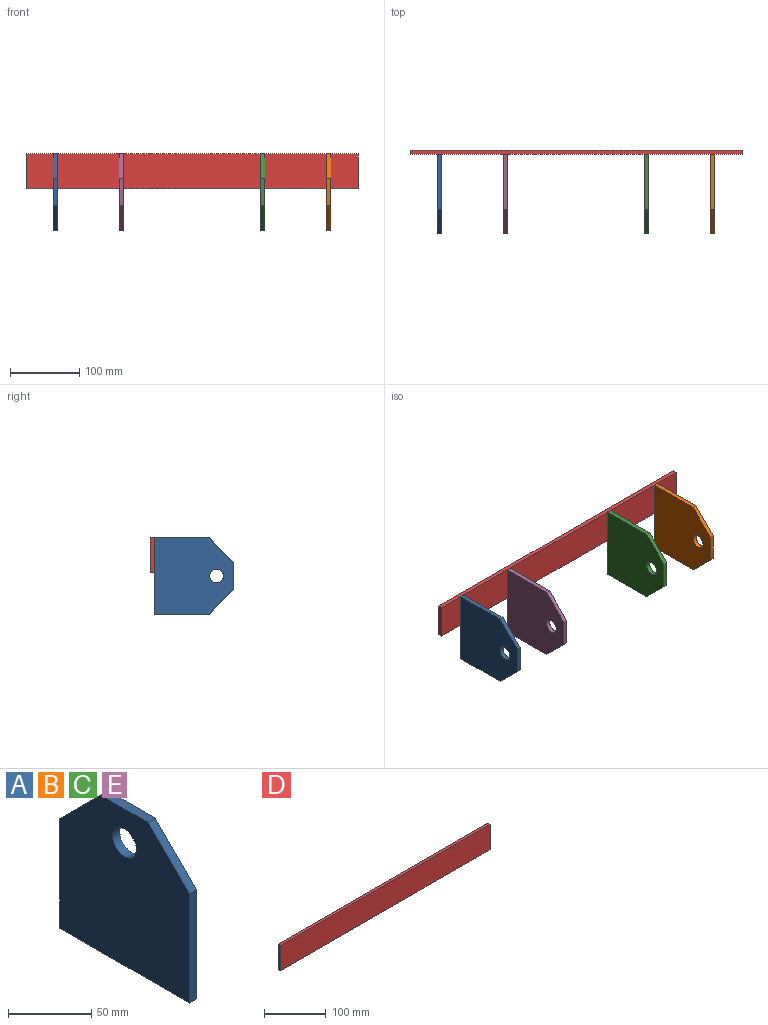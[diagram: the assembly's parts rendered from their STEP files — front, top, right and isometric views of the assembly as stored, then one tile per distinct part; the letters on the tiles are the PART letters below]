
ASSEMBLY  parts=5 mates=4
PART A: 9 faces, bbox 6x110x115 mm
  f0: plane 40x6mm, normal (0,0,1), area 240mm2, adj f1,f5,f7,f8
  f1: plane 35x35mm, normal (0,-0.71,0.71), area 297mm2, adj f0,f2,f7,f8
  f2: plane 80x6mm, normal (0,-1,0), area 480mm2, adj f1,f3,f7,f8
  f3: plane 110x6mm, normal (0,0,-1), area 660mm2, adj f2,f4,f7,f8
  f4: plane 80x6mm, normal (0,1,0), area 480mm2, adj f3,f5,f7,f8
  f5: plane 35x35mm, normal (0,0.71,0.71), area 297mm2, adj f0,f4,f7,f8
  f6: cylinder r=10mm len=20mm, axis (-1,0,0), area 377mm2, adj f7,f8
  f7: plane 115x110mm, normal (1,0,0), area 11110.8mm2, adj f0,f1,f2,f3,f4,f5,f6
  f8: plane 115x110mm, normal (-1,0,0), area 11110.8mm2, adj f0,f1,f2,f3,f4,f5,f6
PART B: same geometry as A
PART C: same geometry as A
PART D: 6 faces, bbox 480x6x50 mm
  f0: plane 480x6mm, normal (0,0,1), area 2880mm2, adj f1,f3,f4,f5
  f1: plane 50x6mm, normal (-1,0,0), area 300mm2, adj f0,f2,f4,f5
  f2: plane 480x6mm, normal (0,0,-1), area 2880mm2, adj f1,f3,f4,f5
  f3: plane 50x6mm, normal (1,0,0), area 300mm2, adj f0,f2,f4,f5
  f4: plane 480x50mm, normal (0,-1,0), area 24000mm2, adj f0,f1,f2,f3
  f5: plane 480x50mm, normal (0,1,0), area 24000mm2, adj f0,f1,f2,f3
PART E: same geometry as A
PLACE A rot(axis=(1,0,0),90deg) t=(-290.32,-37.86,-78.04)mm
PLACE B rot(axis=(1,0,0),90deg) t=(104.68,-37.86,-78.04)mm
PLACE C rot(axis=(1,0,0),90deg) t=(9.68,-37.86,-78.04)mm
PLACE D rot(axis=(1,0,0),180deg) t=(0,-6,-31.92)mm
PLACE E rot(axis=(1,0,0),90deg) t=(-195.32,-37.86,-78.04)mm
MATE fastened C.f3 <-> D.f5  axis (0,1,0) through (12.68,-6,9.04)mm
MATE fastened A.f3 <-> D.f5  axis (0,1,0) through (-287.32,-6,9.04)mm
MATE fastened E.f3 <-> D.f5  axis (0,1,0) through (-192.32,-6,9.04)mm
MATE fastened B.f3 <-> D.f5  axis (0,1,0) through (107.68,-6,9.04)mm
